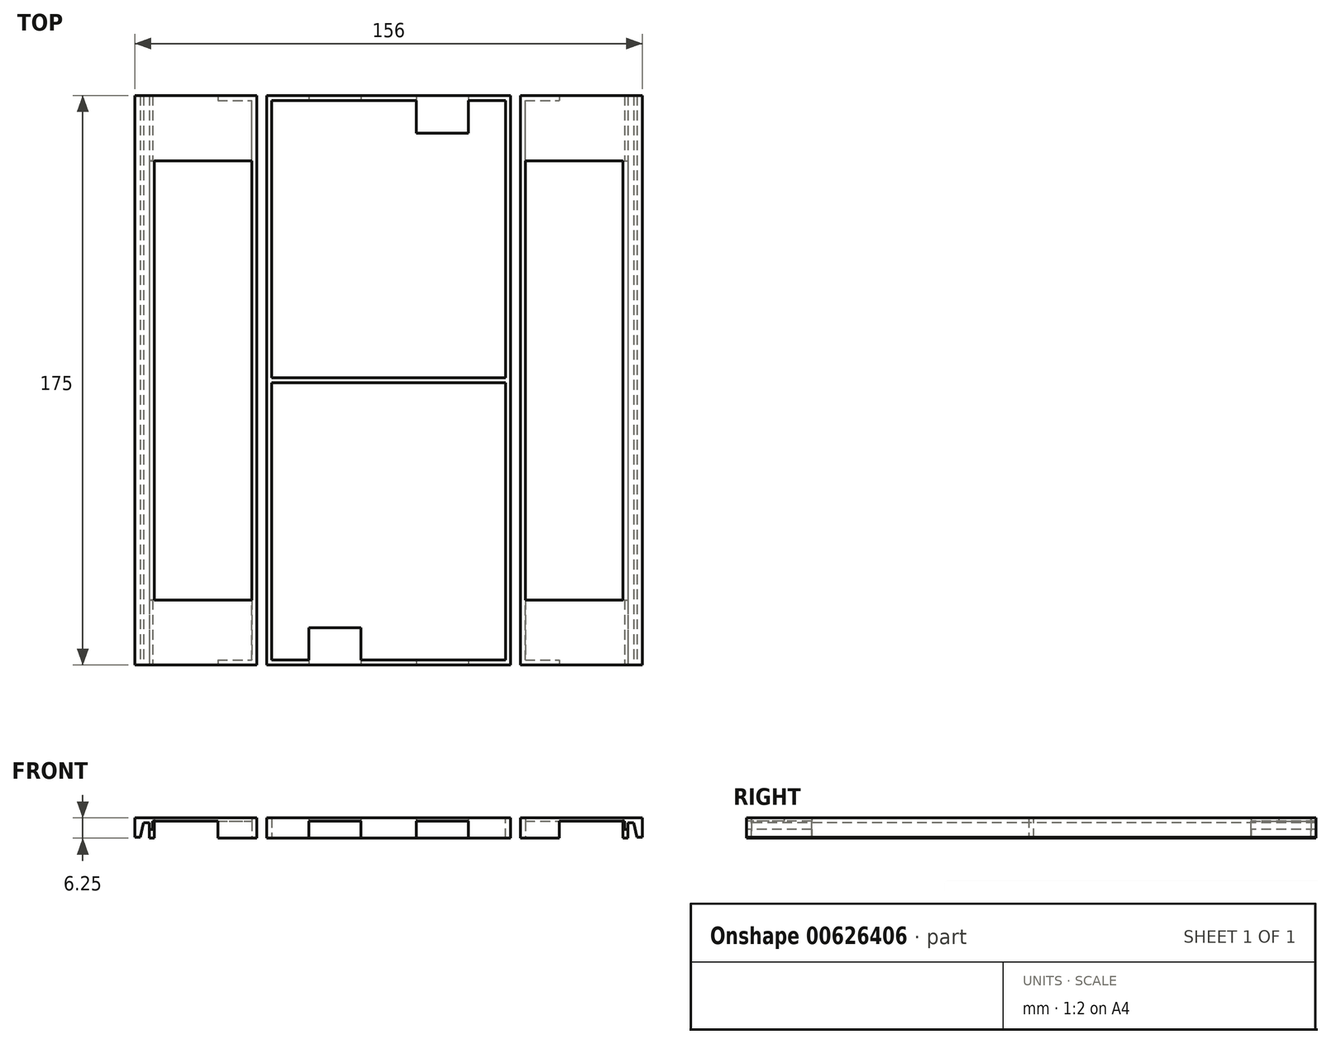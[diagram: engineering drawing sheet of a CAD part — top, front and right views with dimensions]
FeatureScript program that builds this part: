
annotation { "Feature Type Name" : "Feature", "Feature Type Description" : "" }
export const myFeature = defineFeature(function(context is Context, id is Id, definition is map)
    precondition{}
    {
        {
            var Q0;
            Q0=qCreatedBy(makeId("Front.planeOp"),FACE);
            var sketch = newSketch(context, id + "F0", { "sketchPlane" : qUnion([Q0])});
            skLineSegment(sketch, "E0", {"start": v(0, 0.25) * mm, "end": v(0, 6.25) * mm});
            skLineSegment(sketch, "E1", {"start": v(156, 6.25) * mm, "end": v(156, 0.25) * mm});
            skLineSegment(sketch, "E2", {"start": v(156, 0.25) * mm, "end": v(154.3, 0.25) * mm});
            skLineSegment(sketch, "E3", {"start": v(154.3, 0.25) * mm, "end": v(153.3, 4.75) * mm});
            skLineSegment(sketch, "E4", {"start": v(153.3, 4.75) * mm, "end": v(151.5, 4.75) * mm});
            skLineSegment(sketch, "E5", {"start": v(151.5, 4.75) * mm, "end": v(151.5, 0) * mm});
            skLineSegment(sketch, "E6", {"start": v(4.5, 0) * mm, "end": v(4.5, 4.75) * mm});
            skLineSegment(sketch, "E7", {"start": v(4.5, 4.75) * mm, "end": v(2.7, 4.75) * mm});
            skLineSegment(sketch, "E8", {"start": v(2.7, 4.75) * mm, "end": v(1.7, 0.25) * mm});
            skLineSegment(sketch, "E9", {"start": v(1.7, 0.25) * mm, "end": v(0, 0.25) * mm});
            skLineSegment(sketch, "E10", {"start": v(4.5, 0) * mm, "end": v(5.5, 0) * mm});
            skLineSegment(sketch, "E11", {"start": v(5.5, 0) * mm, "end": v(5.5, 5.25) * mm});
            skLineSegment(sketch, "E12", {"start": v(5.5, 5.25) * mm, "end": v(25.5, 5.25) * mm});
            skLineSegment(sketch, "E13", {"start": v(25.5, 5.25) * mm, "end": v(25.5, 0) * mm});
            skLineSegment(sketch, "E14", {"start": v(25.5, 0) * mm, "end": v(37.5, 0) * mm});
            skLineSegment(sketch, "E15", {"start": v(37.5, 0) * mm, "end": v(37.5, 6.25) * mm});
            skLineSegment(sketch, "E16", {"start": v(40.5, 6.25) * mm, "end": v(40.5, 0) * mm});
            skLineSegment(sketch, "E17", {"start": v(40.5, 0) * mm, "end": v(53.5, 0) * mm});
            skLineSegment(sketch, "E18", {"start": v(53.5, 0) * mm, "end": v(53.5, 5.25) * mm});
            skLineSegment(sketch, "E19", {"start": v(53.5, 5.25) * mm, "end": v(69.5, 5.25) * mm});
            skLineSegment(sketch, "E20", {"start": v(69.5, 5.25) * mm, "end": v(69.5, 0) * mm});
            skLineSegment(sketch, "E21", {"start": v(69.5, 0) * mm, "end": v(86.5, 0) * mm});
            skLineSegment(sketch, "E22", {"start": v(86.5, 0) * mm, "end": v(86.5, 5.25) * mm});
            skLineSegment(sketch, "E23", {"start": v(86.5, 5.25) * mm, "end": v(102.5, 5.25) * mm});
            skLineSegment(sketch, "E24", {"start": v(102.5, 5.25) * mm, "end": v(102.5, 0) * mm});
            skLineSegment(sketch, "E25", {"start": v(102.5, 0) * mm, "end": v(115.5, 0) * mm});
            skLineSegment(sketch, "E26", {"start": v(115.5, 0) * mm, "end": v(115.5, 6.25) * mm});
            skLineSegment(sketch, "E27", {"start": v(118.5, 6.25) * mm, "end": v(118.5, 0) * mm});
            skLineSegment(sketch, "E28", {"start": v(118.5, 0) * mm, "end": v(130.5, 0) * mm});
            skLineSegment(sketch, "E29", {"start": v(130.5, 0) * mm, "end": v(130.5, 5.25) * mm});
            skLineSegment(sketch, "E30", {"start": v(130.5, 5.25) * mm, "end": v(150.5, 5.25) * mm});
            skLineSegment(sketch, "E31", {"start": v(150.5, 5.25) * mm, "end": v(150.5, 0) * mm});
            skLineSegment(sketch, "E32", {"start": v(150.5, 0) * mm, "end": v(151.5, 0) * mm});
            skLineSegment(sketch, "E33", {"start": v(0, 6.25) * mm, "end": v(37.5, 6.25) * mm});
            skLineSegment(sketch, "E34", {"start": v(40.5, 6.25) * mm, "end": v(115.5, 6.25) * mm});
            skLineSegment(sketch, "E35", {"start": v(118.5, 6.25) * mm, "end": v(156, 6.25) * mm});
            skSolve(sketch);
        }
        {
            var Q0;
            Q0=makeQuery(id+"F0.imprint","IMPRINT",FACE,{"disambiguationData":[TD([[makeQuery(id+"F0.imprint","IMPRINT",EDGE,{"derivedFrom":sQuery(id+"F0.wireOp",EDGE,"E0")}),-1.0]])]});
            var Q1;
            Q1=makeQuery(id+"F0.imprint","IMPRINT",FACE,{"disambiguationData":[TD([[makeQuery(id+"F0.imprint","IMPRINT",EDGE,{"derivedFrom":sQuery(id+"F0.wireOp",EDGE,"E16")}),1.0]])]});
            var Q2;
            Q2=makeQuery(id+"F0.imprint","IMPRINT",FACE,{"disambiguationData":[TD([[makeQuery(id+"F0.imprint","IMPRINT",EDGE,{"derivedFrom":sQuery(id+"F0.wireOp",EDGE,"E1")}),-1.0]])]});
            extrude(context, id + "F1", {"entities" : qUnion([Q0, Q1, Q2]), "oppositeDirection" : true, "depth" : 175 * mm, "offsetDistance" : 25 * mm});
        }
        {
            var Q0;
            Q0=makeQuery(id+"F1.opExtrude","SWEPT_FACE",FACE,{"disambiguationData":[OSD([sQuery(id+"F0.wireOp",EDGE,"E12")])]});
            var sketch = newSketch(context, id + "F2", { "sketchPlane" : qUnion([Q0])});
            skLineSegment(sketch, "E36.bottom", {"start": v(6, -20) * mm, "end": v(25.5, -20) * mm});
            skLineSegment(sketch, "E36.top", {"start": v(6, -155) * mm, "end": v(25.5, -155) * mm});
            skLineSegment(sketch, "E36.left", {"start": v(6, -20) * mm, "end": v(6, -155) * mm});
            skLineSegment(sketch, "E36.right", {"start": v(25.5, -20) * mm, "end": v(25.5, -155) * mm});
            skSolve(sketch);
        }
        {
            var Q0;
            Q0=makeQuery(id+"F2.imprint","IMPRINT",FACE,{"disambiguationData":[TD([[makeQuery(id+"F2.imprint","IMPRINT",EDGE,{"derivedFrom":sQuery(id+"F2.wireOp",EDGE,"E36.bottom")}),-1.0]])]});
            extrude(context, id + "F3", {"entities" : qUnion([Q0]), "operationType" : NewBodyOperationType.REMOVE, "endBound" : BoundingType.THROUGH_ALL, "oppositeDirection" : true, "depth" : 25 * mm, "offsetDistance" : 25 * mm});
        }
        {
            var Q0;
            Q0=makeQuery(id+"F1.opExtrude","SWEPT_FACE",FACE,{"disambiguationData":[OSD([sQuery(id+"F0.wireOp",EDGE,"E12")])]});
            var sketch = newSketch(context, id + "F4", { "sketchPlane" : qUnion([Q0])});
            skLineSegment(sketch, "E37.bottom", {"start": v(6, -20) * mm, "end": v(5.5, -20) * mm});
            skLineSegment(sketch, "E37.top", {"start": v(6, -155) * mm, "end": v(5.5, -155) * mm});
            skLineSegment(sketch, "E37.left", {"start": v(6, -20) * mm, "end": v(6, -155) * mm});
            skLineSegment(sketch, "E37.right", {"start": v(5.5, -20) * mm, "end": v(5.5, -155) * mm});
            skSolve(sketch);
        }
        {
            var Q0;
            Q0=makeQuery(id+"F4.imprint","IMPRINT",FACE,{"disambiguationData":[TD([[makeQuery(id+"F4.imprint","IMPRINT",EDGE,{"derivedFrom":sQuery(id+"F4.wireOp",EDGE,"E37.bottom")}),1.0]])]});
            extrude(context, id + "F5", {"entities" : qUnion([Q0]), "operationType" : NewBodyOperationType.ADD, "depth" : 5.25 * mm, "offsetDistance" : 25 * mm});
        }
        {
            var Q0;
            Q0=makeQuery(id+"F1.opExtrude","SWEPT_FACE",FACE,{"disambiguationData":[OSD([sQuery(id+"F0.wireOp",EDGE,"E30")])]});
            var sketch = newSketch(context, id + "F6", { "sketchPlane" : qUnion([Q0])});
            skLineSegment(sketch, "E38.bottom", {"start": v(130.5, -20) * mm, "end": v(150, -20) * mm});
            skLineSegment(sketch, "E38.top", {"start": v(130.5, -155) * mm, "end": v(150, -155) * mm});
            skLineSegment(sketch, "E38.left", {"start": v(130.5, -20) * mm, "end": v(130.5, -155) * mm});
            skLineSegment(sketch, "E38.right", {"start": v(150, -20) * mm, "end": v(150, -155) * mm});
            skSolve(sketch);
        }
        {
            var Q0;
            Q0=makeQuery(id+"F6.imprint","IMPRINT",FACE,{"disambiguationData":[TD([[makeQuery(id+"F6.imprint","IMPRINT",EDGE,{"derivedFrom":sQuery(id+"F6.wireOp",EDGE,"E38.bottom")}),-1.0]])]});
            extrude(context, id + "F7", {"entities" : qUnion([Q0]), "operationType" : NewBodyOperationType.REMOVE, "endBound" : BoundingType.THROUGH_ALL, "oppositeDirection" : true, "depth" : 25 * mm, "offsetDistance" : 25 * mm});
        }
        {
            var Q0;
            Q0=makeQuery(id+"F1.opExtrude","SWEPT_FACE",FACE,{"disambiguationData":[OSD([sQuery(id+"F0.wireOp",EDGE,"E30")])]});
            var sketch = newSketch(context, id + "F8", { "sketchPlane" : qUnion([Q0])});
            skLineSegment(sketch, "E39.bottom", {"start": v(150, -20) * mm, "end": v(150.5, -20) * mm});
            skLineSegment(sketch, "E39.top", {"start": v(150, -155) * mm, "end": v(150.5, -155) * mm});
            skLineSegment(sketch, "E39.left", {"start": v(150, -20) * mm, "end": v(150, -155) * mm});
            skLineSegment(sketch, "E39.right", {"start": v(150.5, -20) * mm, "end": v(150.5, -155) * mm});
            skSolve(sketch);
        }
        {
            var Q0;
            Q0=makeQuery(id+"F8.imprint","IMPRINT",FACE,{"disambiguationData":[TD([[makeQuery(id+"F8.imprint","IMPRINT",EDGE,{"derivedFrom":sQuery(id+"F8.wireOp",EDGE,"E39.bottom")}),-1.0]])]});
            extrude(context, id + "F9", {"entities" : qUnion([Q0]), "operationType" : NewBodyOperationType.ADD, "depth" : 5.25 * mm, "offsetDistance" : 25 * mm});
        }
        {
            var Q0;
            Q0=makeQuery(id+"F1.opExtrude","SWEPT_FACE",FACE,{"disambiguationData":[OSD([sQuery(id+"F0.wireOp",EDGE,"E14")])]});
            var sketch = newSketch(context, id + "F10", { "sketchPlane" : qUnion([Q0])});
            skLineSegment(sketch, "E40.bottom", {"start": v(25.5, -20) * mm, "end": v(36, -20) * mm});
            skLineSegment(sketch, "E40.top", {"start": v(25.5, -155) * mm, "end": v(36, -155) * mm});
            skLineSegment(sketch, "E40.left", {"start": v(25.5, -20) * mm, "end": v(25.5, -155) * mm});
            skLineSegment(sketch, "E40.right", {"start": v(36, -20) * mm, "end": v(36, -155) * mm});
            skSolve(sketch);
        }
        {
            var Q0;
            Q0=makeQuery(id+"F10.imprint","IMPRINT",FACE,{"disambiguationData":[TD([[makeQuery(id+"F10.imprint","IMPRINT",EDGE,{"derivedFrom":sQuery(id+"F10.wireOp",EDGE,"E40.bottom")}),-1.0]])]});
            extrude(context, id + "F11", {"entities" : qUnion([Q0]), "operationType" : NewBodyOperationType.REMOVE, "endBound" : BoundingType.THROUGH_ALL, "oppositeDirection" : true, "depth" : 25 * mm, "offsetDistance" : 25 * mm});
        }
        {
            var Q0;
            Q0=makeQuery(id+"F1.opExtrude","SWEPT_FACE",FACE,{"disambiguationData":[OSD([sQuery(id+"F0.wireOp",EDGE,"E14")])]});
            var sketch = newSketch(context, id + "F12", { "sketchPlane" : qUnion([Q0])});
            skLineSegment(sketch, "E41.bottom", {"start": v(25.5, -20) * mm, "end": v(36, -20) * mm});
            skLineSegment(sketch, "E41.top", {"start": v(25.5, -1.5) * mm, "end": v(36, -1.5) * mm});
            skLineSegment(sketch, "E41.left", {"start": v(25.5, -20) * mm, "end": v(25.5, -1.5) * mm});
            skLineSegment(sketch, "E41.right", {"start": v(36, -20) * mm, "end": v(36, -1.5) * mm});
            skLineSegment(sketch, "E42.bottom", {"start": v(25.5, -155) * mm, "end": v(36, -155) * mm});
            skLineSegment(sketch, "E42.top", {"start": v(25.5, -173.5) * mm, "end": v(36, -173.5) * mm});
            skLineSegment(sketch, "E42.left", {"start": v(25.5, -155) * mm, "end": v(25.5, -173.5) * mm});
            skLineSegment(sketch, "E42.right", {"start": v(36, -155) * mm, "end": v(36, -173.5) * mm});
            skSolve(sketch);
        }
        {
            var Q0;
            Q0=makeQuery(id+"F12.imprint","IMPRINT",FACE,{"disambiguationData":[TD([[makeQuery(id+"F12.imprint","IMPRINT",EDGE,{"derivedFrom":sQuery(id+"F12.wireOp",EDGE,"E41.bottom")}),1.0]])]});
            var Q1;
            Q1=makeQuery(id+"F12.imprint","IMPRINT",FACE,{"disambiguationData":[TD([[makeQuery(id+"F12.imprint","IMPRINT",EDGE,{"derivedFrom":sQuery(id+"F12.wireOp",EDGE,"E42.bottom")}),-1.0]])]});
            extrude(context, id + "F13", {"entities" : qUnion([Q0, Q1]), "operationType" : NewBodyOperationType.REMOVE, "oppositeDirection" : true, "depth" : 5.25 * mm, "offsetDistance" : 25 * mm});
        }
        {
            var Q0;
            Q0=makeQuery(id+"F5.boolean.opBoolean","MERGE",FACE,{"derivedFrom":[makeQuery(id+"F1.opExtrude","SWEPT_FACE",FACE,{"disambiguationData":[OSD([sQuery(id+"F0.wireOp",EDGE,"E10")])]}),makeQuery(id+"F5.opExtrude","CAP_FACE",FACE,{"disambiguationData":[OSD([sQuery(id+"F4.wireOp",EDGE,"E37.bottom"),sQuery(id+"F4.wireOp",EDGE,"E37.top"),sQuery(id+"F4.wireOp",EDGE,"E37.left"),sQuery(id+"F4.wireOp",EDGE,"E37.right")])],"isStart":false})]});
            var sketch = newSketch(context, id + "F14", { "sketchPlane" : qUnion([Q0])});
            skLineSegment(sketch, "E43.bottom", {"start": v(4.5, -155) * mm, "end": v(5.5, -155) * mm});
            skLineSegment(sketch, "E43.top", {"start": v(4.5, -175) * mm, "end": v(5.5, -175) * mm});
            skLineSegment(sketch, "E43.left", {"start": v(4.5, -155) * mm, "end": v(4.5, -175) * mm});
            skLineSegment(sketch, "E43.right", {"start": v(5.5, -155) * mm, "end": v(5.5, -175) * mm});
            skLineSegment(sketch, "E44.bottom", {"start": v(4.5, 0) * mm, "end": v(5.5, 0) * mm});
            skLineSegment(sketch, "E44.top", {"start": v(4.5, -20) * mm, "end": v(5.5, -20) * mm});
            skLineSegment(sketch, "E44.left", {"start": v(4.5, 0) * mm, "end": v(4.5, -20) * mm});
            skLineSegment(sketch, "E44.right", {"start": v(5.5, 0) * mm, "end": v(5.5, -20) * mm});
            skSolve(sketch);
        }
        {
            var Q0;
            Q0=makeQuery(id+"F14.imprint","IMPRINT",FACE,{"disambiguationData":[TD([[makeQuery(id+"F14.imprint","IMPRINT",EDGE,{"derivedFrom":sQuery(id+"F14.wireOp",EDGE,"E44.bottom")}),-1.0]])]});
            var Q1;
            Q1=makeQuery(id+"F14.imprint","IMPRINT",FACE,{"disambiguationData":[TD([[makeQuery(id+"F14.imprint","IMPRINT",EDGE,{"derivedFrom":sQuery(id+"F14.wireOp",EDGE,"E43.bottom")}),-1.0]])]});
            extrude(context, id + "F15", {"entities" : qUnion([Q0, Q1]), "operationType" : NewBodyOperationType.REMOVE, "oppositeDirection" : true, "depth" : 2.75 * mm, "offsetDistance" : 25 * mm});
        }
        {
            var Q0;
            Q0=makeQuery(id+"F1.opExtrude","SWEPT_FACE",FACE,{"disambiguationData":[OSD([sQuery(id+"F0.wireOp",EDGE,"E28")])]});
            var sketch = newSketch(context, id + "F16", { "sketchPlane" : qUnion([Q0])});
            skLineSegment(sketch, "E45.bottom", {"start": v(120, -20) * mm, "end": v(130.5, -20) * mm});
            skLineSegment(sketch, "E45.top", {"start": v(120, -155) * mm, "end": v(130.5, -155) * mm});
            skLineSegment(sketch, "E45.left", {"start": v(120, -20) * mm, "end": v(120, -155) * mm});
            skLineSegment(sketch, "E45.right", {"start": v(130.5, -20) * mm, "end": v(130.5, -155) * mm});
            skSolve(sketch);
        }
        {
            var Q0;
            Q0=makeQuery(id+"F16.imprint","IMPRINT",FACE,{"disambiguationData":[TD([[makeQuery(id+"F16.imprint","IMPRINT",EDGE,{"derivedFrom":sQuery(id+"F16.wireOp",EDGE,"E45.bottom")}),-1.0]])]});
            extrude(context, id + "F17", {"entities" : qUnion([Q0]), "operationType" : NewBodyOperationType.REMOVE, "endBound" : BoundingType.THROUGH_ALL, "oppositeDirection" : true, "depth" : 5.25 * mm, "offsetDistance" : 25 * mm});
        }
        {
            var Q0;
            Q0=makeQuery(id+"F1.opExtrude","SWEPT_FACE",FACE,{"disambiguationData":[OSD([sQuery(id+"F0.wireOp",EDGE,"E28")])]});
            var sketch = newSketch(context, id + "F18", { "sketchPlane" : qUnion([Q0])});
            skPoint(sketch, "E46.firstSnap0", {"position": v(125.25, -20) * mm});
            skLineSegment(sketch, "E47.bottom", {"start": v(120, -155) * mm, "end": v(130.5, -155) * mm});
            skLineSegment(sketch, "E47.top", {"start": v(120, -173.5) * mm, "end": v(130.5, -173.5) * mm});
            skLineSegment(sketch, "E47.left", {"start": v(120, -155) * mm, "end": v(120, -173.5) * mm});
            skLineSegment(sketch, "E47.right", {"start": v(130.5, -155) * mm, "end": v(130.5, -173.5) * mm});
            skLineSegment(sketch, "E48.bottom", {"start": v(120, -20) * mm, "end": v(130.5, -20) * mm});
            skLineSegment(sketch, "E48.top", {"start": v(120, -1.5) * mm, "end": v(130.5, -1.5) * mm});
            skLineSegment(sketch, "E48.left", {"start": v(120, -20) * mm, "end": v(120, -1.5) * mm});
            skLineSegment(sketch, "E48.right", {"start": v(130.5, -20) * mm, "end": v(130.5, -1.5) * mm});
            skSolve(sketch);
        }
        {
            var Q0;
            Q0=makeQuery(id+"F18.imprint","IMPRINT",FACE,{"disambiguationData":[TD([[makeQuery(id+"F18.imprint","IMPRINT",EDGE,{"derivedFrom":sQuery(id+"F18.wireOp",EDGE,"E48.bottom")}),1.0]])]});
            var Q1;
            Q1=makeQuery(id+"F18.imprint","IMPRINT",FACE,{"disambiguationData":[TD([[makeQuery(id+"F18.imprint","IMPRINT",EDGE,{"derivedFrom":sQuery(id+"F18.wireOp",EDGE,"E47.bottom")}),-1.0]])]});
            extrude(context, id + "F19", {"entities" : qUnion([Q0, Q1]), "operationType" : NewBodyOperationType.REMOVE, "oppositeDirection" : true, "depth" : 5.25 * mm, "offsetDistance" : 25 * mm});
        }
        {
            var Q0;
            Q0=makeQuery(id+"F9.boolean.opBoolean","MERGE",FACE,{"derivedFrom":[makeQuery(id+"F1.opExtrude","SWEPT_FACE",FACE,{"disambiguationData":[OSD([sQuery(id+"F0.wireOp",EDGE,"E32")])]}),makeQuery(id+"F9.opExtrude","CAP_FACE",FACE,{"disambiguationData":[OSD([sQuery(id+"F8.wireOp",EDGE,"E39.bottom"),sQuery(id+"F8.wireOp",EDGE,"E39.top"),sQuery(id+"F8.wireOp",EDGE,"E39.left"),sQuery(id+"F8.wireOp",EDGE,"E39.right")])],"isStart":false})]});
            var sketch = newSketch(context, id + "F20", { "sketchPlane" : qUnion([Q0])});
            skLineSegment(sketch, "E49.bottom", {"start": v(150.5, -20) * mm, "end": v(151.5, -20) * mm});
            skLineSegment(sketch, "E49.top", {"start": v(150.5, 0) * mm, "end": v(151.5, 0) * mm});
            skLineSegment(sketch, "E49.left", {"start": v(150.5, -20) * mm, "end": v(150.5, 0) * mm});
            skLineSegment(sketch, "E49.right", {"start": v(151.5, -20) * mm, "end": v(151.5, 0) * mm});
            skLineSegment(sketch, "E50.bottom", {"start": v(150.5, -155) * mm, "end": v(151.5, -155) * mm});
            skLineSegment(sketch, "E50.top", {"start": v(150.5, -175) * mm, "end": v(151.5, -175) * mm});
            skLineSegment(sketch, "E50.left", {"start": v(150.5, -155) * mm, "end": v(150.5, -175) * mm});
            skLineSegment(sketch, "E50.right", {"start": v(151.5, -155) * mm, "end": v(151.5, -175) * mm});
            skSolve(sketch);
        }
        {
            var Q0;
            Q0=makeQuery(id+"F20.imprint","IMPRINT",FACE,{"disambiguationData":[TD([[makeQuery(id+"F20.imprint","IMPRINT",EDGE,{"derivedFrom":sQuery(id+"F20.wireOp",EDGE,"E49.bottom")}),1.0]])]});
            var Q1;
            Q1=makeQuery(id+"F20.imprint","IMPRINT",FACE,{"disambiguationData":[TD([[makeQuery(id+"F20.imprint","IMPRINT",EDGE,{"derivedFrom":sQuery(id+"F20.wireOp",EDGE,"E50.bottom")}),-1.0]])]});
            extrude(context, id + "F21", {"entities" : qUnion([Q0, Q1]), "operationType" : NewBodyOperationType.REMOVE, "oppositeDirection" : true, "depth" : 2.75 * mm, "offsetDistance" : 25 * mm});
        }
        {
            var Q0;
            Q0=makeQuery(id+"F1.opExtrude","SWEPT_FACE",FACE,{"disambiguationData":[OSD([sQuery(id+"F0.wireOp",EDGE,"E34")])]});
            var sketch = newSketch(context, id + "F22", { "sketchPlane" : qUnion([Q0])});
            skLineSegment(sketch, "E51.bottom", {"start": v(42, 173.5) * mm, "end": v(114, 173.5) * mm});
            skLineSegment(sketch, "E51.top", {"start": v(42, 1.5) * mm, "end": v(114, 1.5) * mm});
            skLineSegment(sketch, "E51.left", {"start": v(42, 173.5) * mm, "end": v(42, 1.5) * mm});
            skLineSegment(sketch, "E51.right", {"start": v(114, 173.5) * mm, "end": v(114, 1.5) * mm});
            skSolve(sketch);
        }
        {
            var Q0;
            Q0=makeQuery(id+"F22.imprint","IMPRINT",FACE,{"disambiguationData":[TD([[makeQuery(id+"F22.imprint","IMPRINT",EDGE,{"derivedFrom":sQuery(id+"F22.wireOp",EDGE,"E51.bottom")}),-1.0]])]});
            extrude(context, id + "F23", {"entities" : qUnion([Q0]), "operationType" : NewBodyOperationType.REMOVE, "endBound" : BoundingType.THROUGH_ALL, "oppositeDirection" : true, "depth" : 25 * mm, "offsetDistance" : 25 * mm});
        }
        {
            var Q0;
            Q0=makeQuery(id+"F23.boolean.opBoolean","COPY",FACE,{"derivedFrom":makeQuery(id+"F23.opExtrude","SWEPT_FACE",FACE,{"disambiguationData":[OSD([sQuery(id+"F22.wireOp",EDGE,"E51.left")])]})});
            var sketch = newSketch(context, id + "F24", { "sketchPlane" : qUnion([Q0])});
            skLineSegment(sketch, "E52.bottom", {"start": v(86.75, 6.25) * mm, "end": v(88.25, 6.25) * mm});
            skLineSegment(sketch, "E52.top", {"start": v(86.75, 0) * mm, "end": v(88.25, 0) * mm});
            skLineSegment(sketch, "E52.left", {"start": v(86.75, 6.25) * mm, "end": v(86.75, 0) * mm});
            skLineSegment(sketch, "E52.right", {"start": v(88.25, 6.25) * mm, "end": v(88.25, 0) * mm});
            skSolve(sketch);
        }
        {
            var Q0;
            Q0=makeQuery(id+"F24.imprint","IMPRINT",FACE,{"disambiguationData":[TD([[makeQuery(id+"F24.imprint","IMPRINT",EDGE,{"derivedFrom":sQuery(id+"F24.wireOp",EDGE,"E52.bottom")}),1.0]])]});
            extrude(context, id + "F25", {"entities" : qUnion([Q0]), "operationType" : NewBodyOperationType.ADD, "endBound" : BoundingType.UP_TO_NEXT, "depth" : 25 * mm, "offsetDistance" : 25 * mm});
        }
        {
            var Q0;
            Q0=makeQuery(id+"F23.boolean.opBoolean","COPY",FACE,{"derivedFrom":makeQuery(id+"F23.opExtrude","SWEPT_FACE",FACE,{"disambiguationData":[OSD([sQuery(id+"F22.wireOp",EDGE,"E51.bottom")])]})});
            var sketch = newSketch(context, id + "F26", { "sketchPlane" : qUnion([Q0])});
            skLineSegment(sketch, "E53.bottom", {"start": v(86.5, 6.25) * mm, "end": v(102.5, 6.25) * mm});
            skLineSegment(sketch, "E53.top", {"start": v(86.5, 5.25) * mm, "end": v(102.5, 5.25) * mm});
            skLineSegment(sketch, "E53.left", {"start": v(86.5, 6.25) * mm, "end": v(86.5, 5.25) * mm});
            skLineSegment(sketch, "E53.right", {"start": v(102.5, 6.25) * mm, "end": v(102.5, 5.25) * mm});
            skSolve(sketch);
        }
        {
            var Q0;
            Q0=makeQuery(id+"F26.imprint","IMPRINT",FACE,{"disambiguationData":[TD([[makeQuery(id+"F26.imprint","IMPRINT",EDGE,{"derivedFrom":sQuery(id+"F26.wireOp",EDGE,"E53.bottom")}),-1.0]])]});
            extrude(context, id + "F27", {"entities" : qUnion([Q0]), "operationType" : NewBodyOperationType.ADD, "depth" : 10 * mm, "offsetDistance" : 25 * mm});
        }
        {
            var Q0;
            Q0=makeQuery(id+"F23.boolean.opBoolean","COPY",FACE,{"derivedFrom":makeQuery(id+"F23.opExtrude","SWEPT_FACE",FACE,{"disambiguationData":[OSD([sQuery(id+"F22.wireOp",EDGE,"E51.top")])]})});
            var sketch = newSketch(context, id + "F28", { "sketchPlane" : qUnion([Q0])});
            skLineSegment(sketch, "E54.bottom", {"start": v(-69.5, 6.25) * mm, "end": v(-53.5, 6.25) * mm});
            skLineSegment(sketch, "E54.top", {"start": v(-69.5, 5.25) * mm, "end": v(-53.5, 5.25) * mm});
            skLineSegment(sketch, "E54.left", {"start": v(-69.5, 6.25) * mm, "end": v(-69.5, 5.25) * mm});
            skLineSegment(sketch, "E54.right", {"start": v(-53.5, 6.25) * mm, "end": v(-53.5, 5.25) * mm});
            skSolve(sketch);
        }
        {
            var Q0;
            Q0=makeQuery(id+"F28.imprint","IMPRINT",FACE,{"disambiguationData":[TD([[makeQuery(id+"F28.imprint","IMPRINT",EDGE,{"derivedFrom":sQuery(id+"F28.wireOp",EDGE,"E54.bottom")}),1.0]])]});
            extrude(context, id + "F29", {"entities" : qUnion([Q0]), "operationType" : NewBodyOperationType.ADD, "depth" : 10 * mm, "offsetDistance" : 25 * mm});
        }
    });
